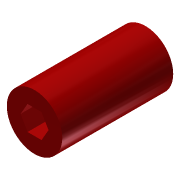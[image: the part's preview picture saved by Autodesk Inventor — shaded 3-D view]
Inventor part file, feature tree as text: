
AUTODESK INVENTOR PART (.ipt)
format: ipt  version: 2014 SP2 (Build 180246200, 246)  size: 107,008 bytes
history: native  units: in
note: dims shown in document units (in); Inventor stores cm internally (conversion verified against a paired STEP export)
features: extrude x2, sketch x2
ambient origin geometry x8: Origin, YZ Plane, XZ Plane, XY Plane, X Axis, Y Axis, Z Axis, Center Point
bodies: Solid1 (feature_tree)
feature tree (4):
  extrude  "Extrusion1"  Depth=1.0in
  extrude  "Extrusion2"  Depth=1.0in TaperAngle=0.0deg
  sketch  "Sketch1"  dims[d0=0.394in d1=1.0in]
  sketch  "Sketch2"  dims[d5=0.095in d6=1.0in d7=0.0in d8=0.4375in d9=1.0in d10=0.0in]
